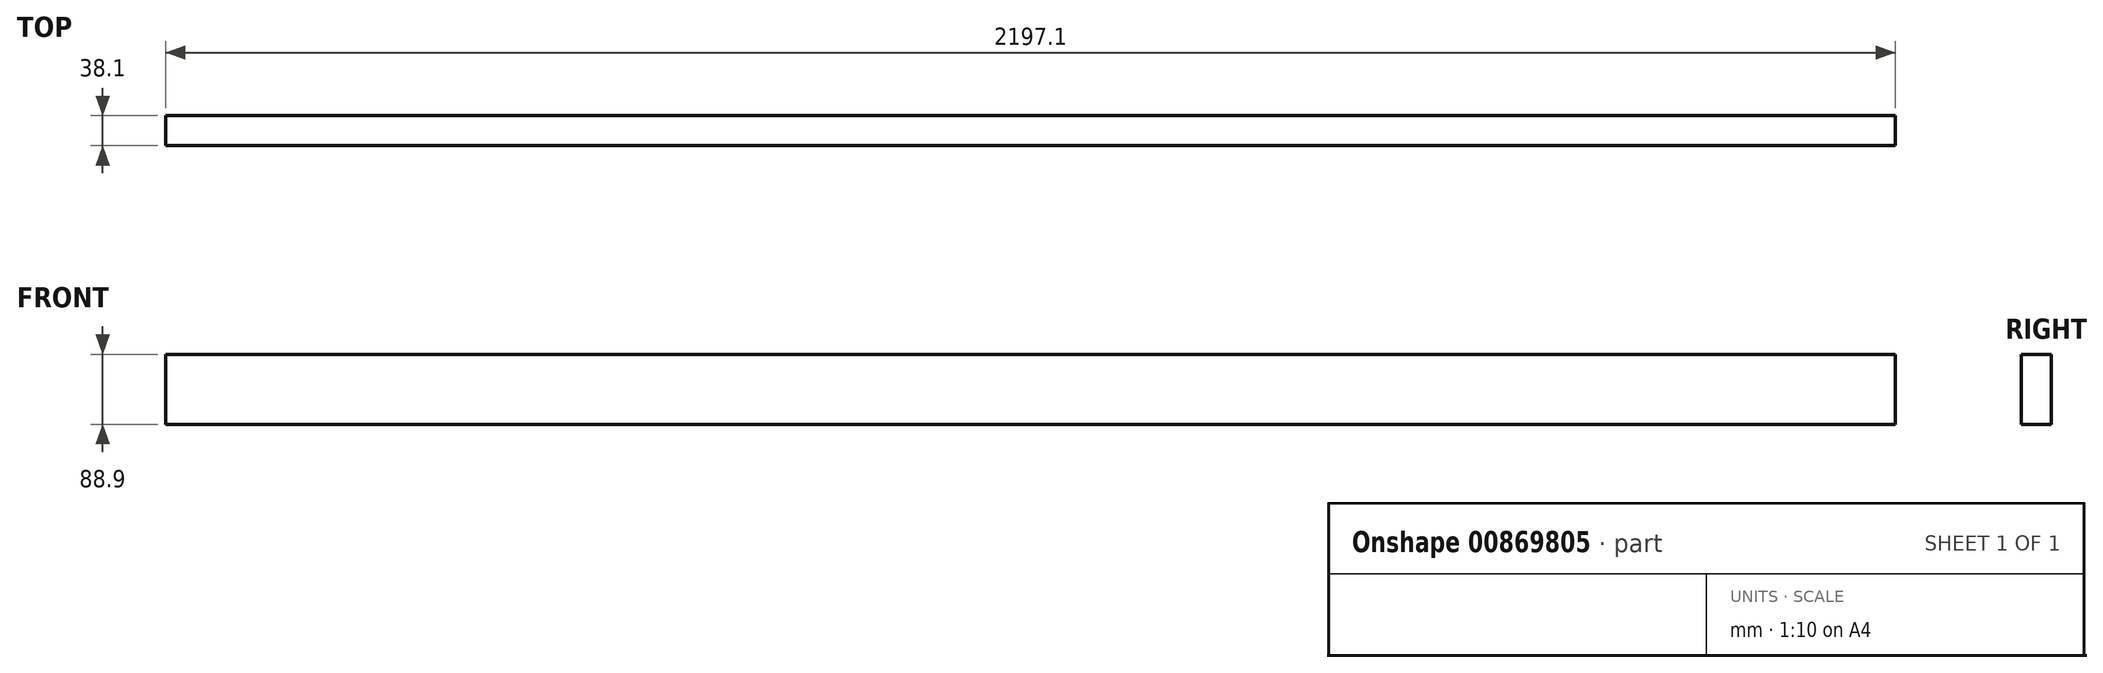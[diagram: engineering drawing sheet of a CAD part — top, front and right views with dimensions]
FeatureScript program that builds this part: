
annotation { "Feature Type Name" : "Feature", "Feature Type Description" : "" }
export const myFeature = defineFeature(function(context is Context, id is Id, definition is map)
    precondition{}
    {
        {
            var Q0;
            Q0=qCreatedBy(makeId("Top.planeOp"),FACE);
            var sketch = newSketch(context, id + "F0", { "sketchPlane" : qUnion([Q0])});
            skLineSegment(sketch, "E0.bottom", {"start": v(0, 0) * mm, "end": v(2197.1, 0) * mm});
            skLineSegment(sketch, "E0.top", {"start": v(0, -38.1) * mm, "end": v(2197.1, -38.1) * mm});
            skLineSegment(sketch, "E0.left", {"start": v(0, 0) * mm, "end": v(0, -38.1) * mm});
            skLineSegment(sketch, "E0.right", {"start": v(2197.1, 0) * mm, "end": v(2197.1, -38.1) * mm});
            skSolve(sketch);
        }
        {
            var Q0;
            Q0 = qSketchRegion(id + "F0", true);
            extrude(context, id + "F1", {"entities" : qUnion([Q0]), "depth" : 88.9 * mm, "offsetDistance" : 25.4 * mm});
        }
    });
